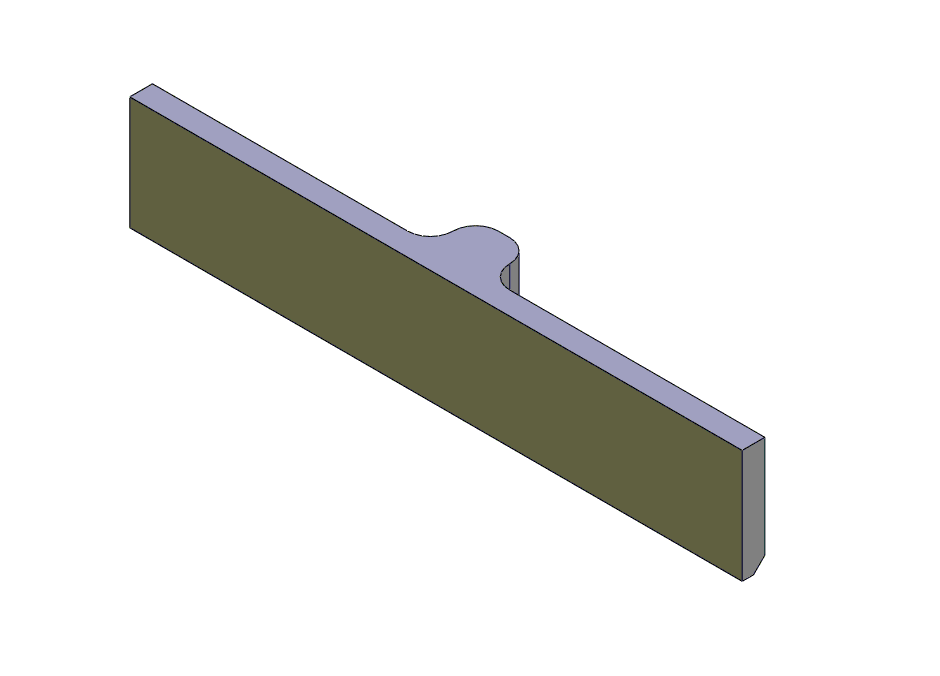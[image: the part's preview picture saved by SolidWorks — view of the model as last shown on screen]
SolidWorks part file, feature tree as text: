
SOLIDWORKS PART (.sldprt)
format: sldprt  version: not decoded by parser v0  size: 291,328 bytes
history: native  units: mm
features: sketch x5, extrude x5, fillet x2, material x1, chamfer x1 (+11 scaffold rows collapsed)
feature tree (25):
  scaffold x11  (default folders/planes/origin — collapsed)
  material  "Material <not specified>"
  sketch  "Sketch1"  dims[D1=137.16mm D2=25.4mm]
  extrude  "Boss-Extrude1"  Depth=5.08mm
  sketch  "Sketch2"  dims[D1=12.7mm D2=62.23mm D3=3.81mm]
  extrude  "Boss-Extrude2"  Depth=10.16mm
  sketch  "Sketch3"  dims[D1=12.7mm D2=6.35mm D3=6.35mm D4=6.35mm D5=12.7mm D6=12.7mm D7=6.35mm D8=6.35mm D9=6.35mm D10=12.7mm D11=6.35mm D12=6.35mm]
  extrude  "Boss-Extrude3"  Depth=3.81mm
  sketch  "Sketch4"  dims[c1.D1=0.0mm c1.D2=1.27mm c1.D3=1.27mm c1.D4=1.27mm c1.D5=1.27mm c1.D6=1.27mm c1.D7=12.7mm c2.D7=90.0deg c3.D7=1.27mm c3.D8=1.27mm c3.D9=1.27mm c3.D10=1.27mm c3.D11=0.0mm c3.D12=1.27mm c3.D13=1.27mm c3.D14=1.27mm c3.D15=1.27mm c3.D16=1.27mm c3.D17=0.0mm]
  extrude  "Boss-Extrude4"  Depth=0.635mm
  fillet  "Fillet1"  Radius=5.08mm
  fillet  "Fillet2"  Radius=5.08mm
  chamfer  "Chamfer1"  Distance=2.54mm Angle=45deg
  sketch  "Sketch5"  dims[c1.D1=3.81mm c1.D2=3.81mm c1.D3=3.81mm c1.D4=3.81mm c1.D5=22.86mm c1.D6=30.48mm c1.D7=30.48mm c1.D8=22.86mm c1.D9=1.905mm c1.D10=1.905mm c1.D11=1.905mm c1.D12=1.905mm c1.D13=27.94mm c2.D5=30.48mm]
  extrude  "Boss-Extrude5"  Depth=10.16mm
decode coverage: 13 of 13 modeling features carry decoded parameters
note: suppression state not decoded; provenance and decode notes live in map.json
